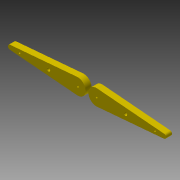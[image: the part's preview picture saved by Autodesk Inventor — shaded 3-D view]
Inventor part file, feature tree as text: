
AUTODESK INVENTOR PART (.ipt)
format: ipt  version: 2015 (Build 190159000, 159)  size: 104,960 bytes
history: native  units: in
note: dims shown in document units (in); Inventor stores cm internally (conversion verified against a paired STEP export)
features: extrude x1, sketch x1
ambient origin geometry x8: Origin, YZ Plane, XZ Plane, XY Plane, X Axis, Y Axis, Z Axis, Center Point
bodies: Solid1 (feature_tree)
feature tree (2):
  extrude  "Extrusion1"  Depth=0.1181in
  sketch  "Sketch1"  dims[d0=0.315in d1=0.315in d2=0.1181in d3=0.0in]
